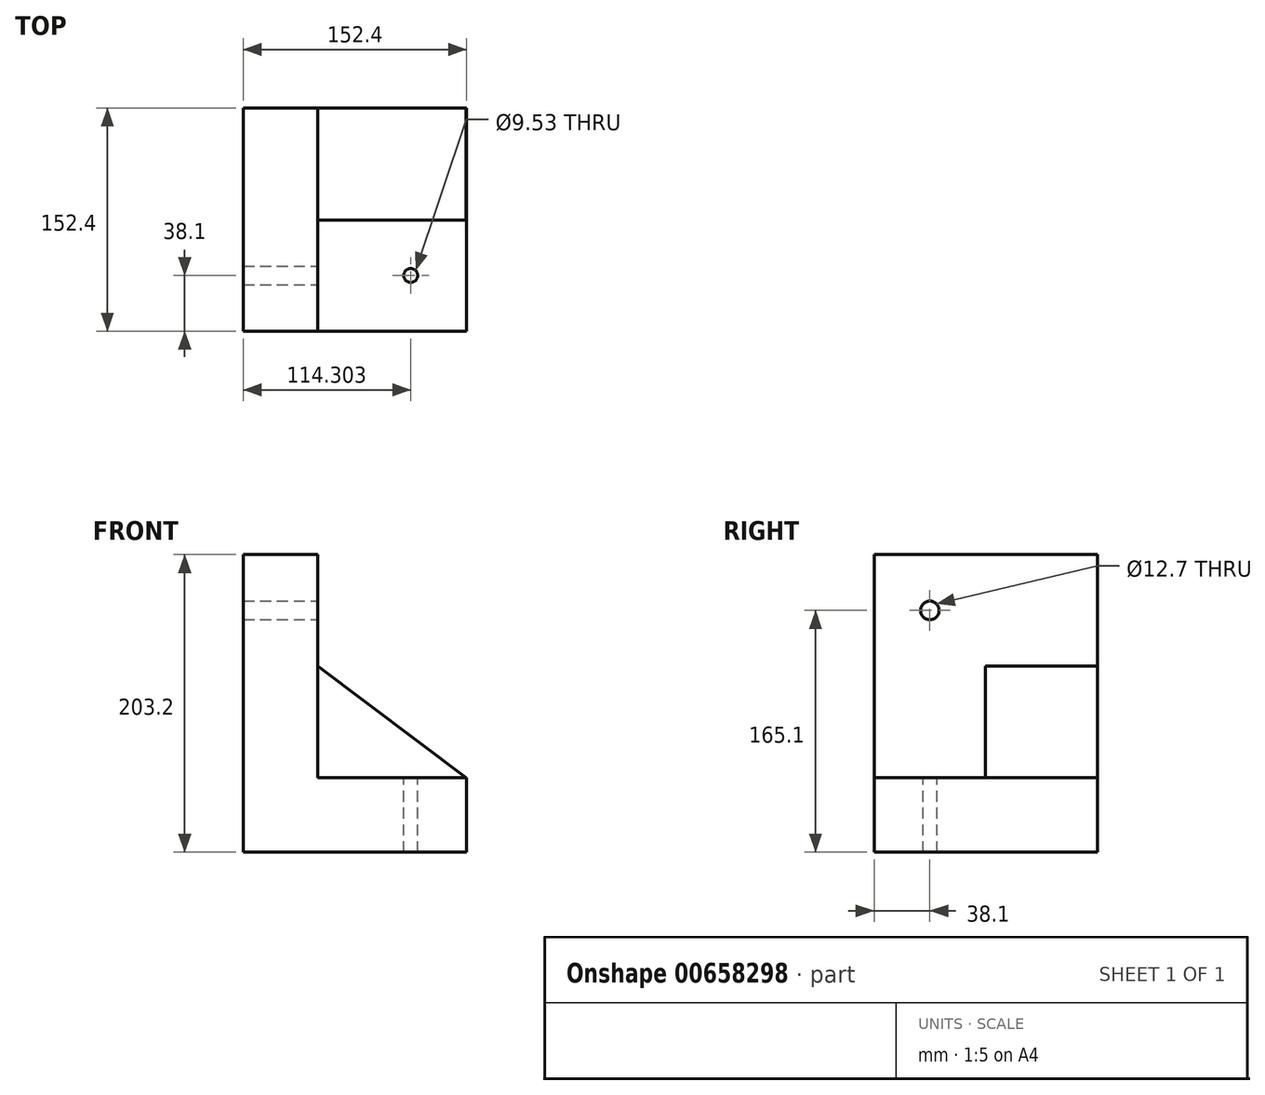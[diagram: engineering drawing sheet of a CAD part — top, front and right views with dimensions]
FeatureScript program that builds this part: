
annotation { "Feature Type Name" : "Feature", "Feature Type Description" : "" }
export const myFeature = defineFeature(function(context is Context, id is Id, definition is map)
    precondition{}
    {
        {
            var Q0;
            Q0=qCreatedBy(makeId("Front.planeOp"),FACE);
            var sketch = newSketch(context, id + "F0", { "sketchPlane" : qUnion([Q0])});
            skLineSegment(sketch, "E0", {"start": v(28.82, 152.4) * mm, "end": v(-21.98, 152.4) * mm});
            skLineSegment(sketch, "E1", {"start": v(-21.98, 152.4) * mm, "end": v(-21.98, -50.8) * mm});
            skLineSegment(sketch, "E2", {"start": v(-21.98, -50.8) * mm, "end": v(130.42, -50.8) * mm});
            skLineSegment(sketch, "E3", {"start": v(130.42, -50.8) * mm, "end": v(130.42, 0) * mm});
            skLineSegment(sketch, "E4", {"start": v(130.42, 0) * mm, "end": v(28.82, 0) * mm});
            skLineSegment(sketch, "E5", {"start": v(28.82, 0) * mm, "end": v(28.82, 152.4) * mm});
            skSolve(sketch);
        }
        {
            var Q0;
            Q0=makeQuery(id+"F0.imprint","IMPRINT",FACE,{"disambiguationData":[TD([[makeQuery(id+"F0.imprint","IMPRINT",EDGE,{"derivedFrom":sQuery(id+"F0.wireOp",EDGE,"E0")}),1.0]])]});
            extrude(context, id + "F1", {"entities" : qUnion([Q0]), "depth" : 152.4 * mm, "offsetDistance" : 25.4 * mm});
        }
        {
            var Q0;
            Q0=makeQuery(id+"F1.opExtrude","SWEPT_FACE",FACE,{"disambiguationData":[OSD([sQuery(id+"F0.wireOp",EDGE,"E4")])]});
            var sketch = newSketch(context, id + "F2", { "sketchPlane" : qUnion([Q0])});
            skLineSegment(sketch, "E6.bottom", {"start": v(28.82, 0) * mm, "end": v(130.18, 0) * mm});
            skLineSegment(sketch, "E6.top", {"start": v(28.82, -76.4) * mm, "end": v(130.18, -76.4) * mm});
            skLineSegment(sketch, "E6.left", {"start": v(28.82, 0) * mm, "end": v(28.82, -76.4) * mm});
            skLineSegment(sketch, "E6.right", {"start": v(130.18, 0) * mm, "end": v(130.18, -76.4) * mm});
            skSolve(sketch);
        }
        {
            var Q0;
            Q0 = qSketchRegion(id + "F2", true);
            extrude(context, id + "F3", {"entities" : qUnion([Q0]), "operationType" : NewBodyOperationType.ADD, "depth" : 76.2 * mm, "offsetDistance" : 25.4 * mm});
        }
        {
            var Q0;
            Q0=makeQuery(id+"F3.opExtrude","SWEPT_FACE",FACE,{"disambiguationData":[OSD([sQuery(id+"F2.wireOp",EDGE,"E6.top")])]});
            var sketch = newSketch(context, id + "F4", { "sketchPlane" : qUnion([Q0])});
            skLineSegment(sketch, "E7", {"start": v(28.82, 76.2) * mm, "end": v(130.18, 0) * mm});
            skLineSegment(sketch, "E8", {"start": v(130.18, 0) * mm, "end": v(28.82, 0) * mm});
            skLineSegment(sketch, "E9", {"start": v(28.82, 0) * mm, "end": v(28.82, 76.2) * mm});
            skSolve(sketch);
        }
        {
            var Q0;
            Q0=makeQuery(id+"F4.imprint","IMPRINT",FACE,{"disambiguationData":[TD([[makeQuery(id+"F4.imprint","IMPRINT",EDGE,{"derivedFrom":sQuery(id+"F4.wireOp",EDGE,"E7")}),1.0]])]});
            extrude(context, id + "F5", {"entities" : qUnion([Q0]), "operationType" : NewBodyOperationType.REMOVE, "oppositeDirection" : true, "depth" : 84.1 * mm, "offsetDistance" : 25.4 * mm});
        }
        {
            var Q0;
            {var subQ3=sQuery(id+"F2.wireOp",EDGE,"E6.top");Q0=makeQuery(id+"F2.imprint","IMPRINT",FACE,{"disambiguationData":[TD([[makeQuery(id+"F2.imprint","IMPRINT",EDGE,{"derivedFrom":subQ3}),-1.0]])]});}
            var sketch = newSketch(context, id + "F6", { "sketchPlane" : qUnion([Q0])});
            skCircle(sketch, "E10", {"center": v(92.32, -114.3) * mm, "radius": 4.76 * mm});
            skSolve(sketch);
        }
        {
            var Q0;
            Q0=sQuery(id+"F6.wireOp",VERTEX,"E10.center");
            var Q1;
            Q1=makeQuery(id+"F1.opExtrude","SWEPT_BODY",BODY,{"disambiguationData":[OSD([sQuery(id+"F0.wireOp",EDGE,"E0"),sQuery(id+"F0.wireOp",EDGE,"E1"),sQuery(id+"F0.wireOp",EDGE,"E2"),sQuery(id+"F0.wireOp",EDGE,"E3"),sQuery(id+"F0.wireOp",EDGE,"E4"),sQuery(id+"F0.wireOp",EDGE,"E5")])]});
            hole(context, id + "F7", {"style" : HoleStyle.SIMPLE, "endStyle" : HoleEndStyle.THROUGH, "holeDiameter" : 9.52 * mm, "majorDiameter" : 6.35 * mm, "isTappedThrough" : true, "tappedDepth" : 12.7 * mm, "tapClearance" : 3, "locations" : qUnion([Q0]), "scope" : qUnion([Q1])});
        }
        {
            var Q0;
            Q0=makeQuery(id+"F1.opExtrude","SWEPT_FACE",FACE,{"disambiguationData":[OSD([sQuery(id+"F0.wireOp",EDGE,"E5")])]});
            var sketch = newSketch(context, id + "F8", { "sketchPlane" : qUnion([Q0])});
            skPoint(sketch, "E11", {"position": v(-114.3, 114.3) * mm});
            skSolve(sketch);
        }
        {
            var Q0;
            Q0=sQuery(id+"F8.wireOp",VERTEX,"E11");
            var Q1;
            Q1=makeQuery(id+"F1.opExtrude","SWEPT_BODY",BODY,{"disambiguationData":[OSD([sQuery(id+"F0.wireOp",EDGE,"E0"),sQuery(id+"F0.wireOp",EDGE,"E1"),sQuery(id+"F0.wireOp",EDGE,"E2"),sQuery(id+"F0.wireOp",EDGE,"E3"),sQuery(id+"F0.wireOp",EDGE,"E4"),sQuery(id+"F0.wireOp",EDGE,"E5")])]});
            hole(context, id + "F9", {"style" : HoleStyle.SIMPLE, "endStyle" : HoleEndStyle.THROUGH, "holeDiameter" : 12.7 * mm, "majorDiameter" : 6.35 * mm, "isTappedThrough" : true, "tappedDepth" : 12.7 * mm, "tapClearance" : 3, "locations" : qUnion([Q0]), "scope" : qUnion([Q1])});
        }
    });
